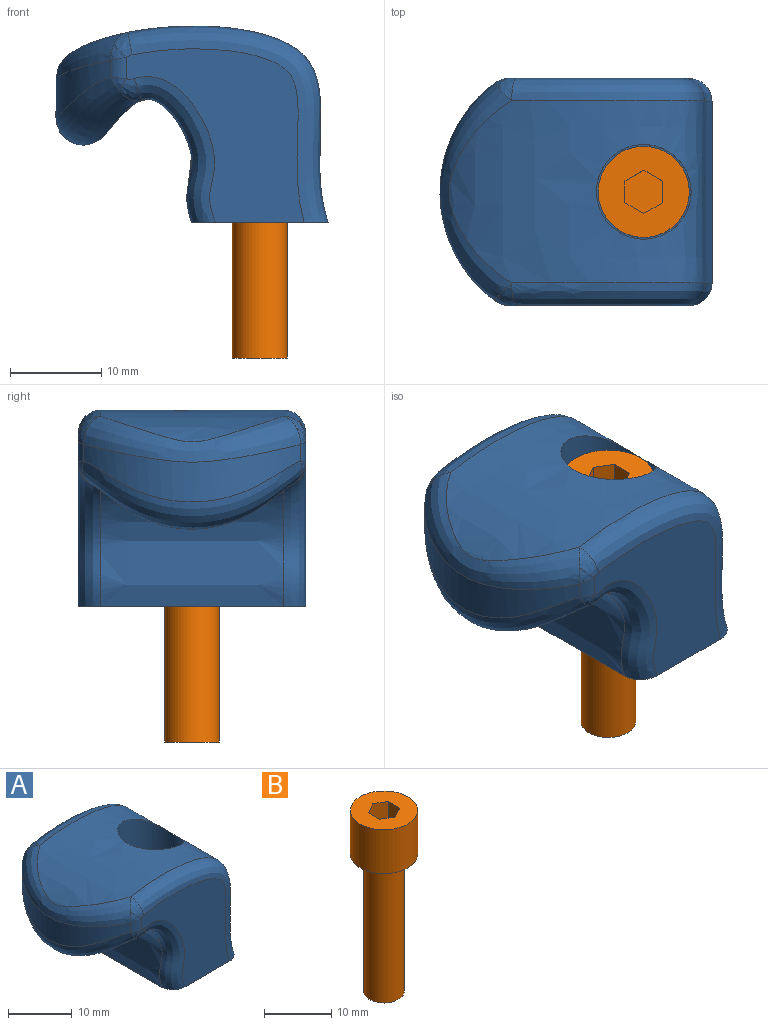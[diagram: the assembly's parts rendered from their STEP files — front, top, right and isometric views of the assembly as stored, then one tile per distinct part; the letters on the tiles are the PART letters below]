
ASSEMBLY  parts=2 mates=1
PART A: 25 faces, bbox 30.5x26.9x25.8 mm
  f0: extruded ~20x13.5mm, area 328.2mm2, adj f4,f11,f12,f15
  f1: extruded ~28.88x21.55mm, area 787mm2, adj f4,f5,f9,f10,f23
  f2: plane 19.51x19.07mm, normal (0,-1,0), area 211.6mm2, adj f4,f9,f12,f14,f19,f24
  f3: plane 19.51x19.07mm, normal (0,1,0), area 211.6mm2, adj f4,f10,f11,f13,f18,f21
  f4: plane 25.36x15.36mm, normal (0,0,-1), area 341.1mm2, adj f0,f1,f2,f3,f7,f9,f10,f11
  f5: cylinder r=5.2mm len=10.4mm, axis (0,0,1), area 258.7mm2, adj f1,f6
  f6: plane 10.4x10.4mm, normal (0,0,1), area 56.7mm2, adj f5,f7
  f7: cylinder r=3mm len=10mm, axis (0,0,1), area 188.5mm2, adj f4,f6
  f8: cylinder r=14.88mm len=23.8mm, axis (0,0,1), area 93.9mm2, adj f15,f18,f19,f23
  f9: bspline ~23.08x22.86mm, area 146.3mm2, adj f1,f2,f4,f24
  f10: bspline ~23.08x22.86mm, area 146.3mm2, adj f1,f3,f4,f21
  f11: bspline ~19.91x10.37mm, area 71.6mm2, adj f0,f3,f4,f13
  f12: bspline ~19.91x10.37mm, area 71.6mm2, adj f0,f2,f4,f14
  f13: bspline ~3.05x3.01mm, area 5mm2, adj f3,f11,f15,f16
  f14: bspline ~3.22x3.01mm, area 5mm2, adj f2,f12,f15,f17
  f15: bspline ~26.46x13.18mm, area 190.1mm2, adj f0,f8,f13,f14,f16,f17
  f16: bspline ~2.45x2.04mm, area 1.1mm2, adj f13,f15,f18
  f17: bspline ~2.45x2.04mm, area 1.1mm2, adj f14,f15,f19
  f18: cylinder r=3mm len=2.33mm, axis (0,0,1), area 4mm2, adj f3,f8,f16,f20
  f19: cylinder r=3mm len=2.33mm, axis (0,0,1), area 4mm2, adj f2,f8,f17,f22
  f20: bspline ~2.18x2.1mm, area 1.3mm2, adj f18,f21,f23
  f21: bspline ~3.18x2.85mm, area 4.5mm2, adj f3,f10,f20,f23
  f22: bspline ~2.18x2.1mm, area 1.3mm2, adj f19,f23,f24
  f23: bspline ~26.37x8.94mm, area 95.3mm2, adj f1,f8,f20,f21,f22,f24
  f24: bspline ~2.98x2.66mm, area 4.5mm2, adj f2,f9,f22,f23
PART B: 12 faces, bbox 10x10x33 mm
  f0: plane 10x10mm, normal (0,0,1), area 63.7mm2, adj f3,f5,f6,f7,f8,f9,f10
  f1: cylinder r=3mm len=25mm, axis (0,0,-1), area 471.2mm2, adj f2,f4
  f2: plane 6x6mm, normal (0,0,-1), area 28.3mm2, adj f1
  f3: cylinder r=5mm len=10mm, axis (0,0,-1), area 251.3mm2, adj f0,f4
  f4: plane 10x10mm, normal (0,0,-1), area 50.3mm2, adj f1,f3
  f5: plane 7x2.08mm, normal (-0.49,0.87,0), area 16.7mm2, adj f0,f6,f10,f11
  f6: plane 7x2.39mm, normal (-1,0.01,0), area 16.7mm2, adj f0,f5,f7,f11
  f7: plane 7x2.06mm, normal (-0.51,-0.86,0), area 16.7mm2, adj f0,f6,f8,f11
  f8: plane 7x2.08mm, normal (0.49,-0.87,0), area 16.7mm2, adj f0,f7,f9,f11
  f9: plane 7x2.39mm, normal (1,-0.01,0), area 16.7mm2, adj f0,f8,f10,f11
  f10: plane 7x2.06mm, normal (0.51,0.86,0), area 16.7mm2, adj f0,f5,f9,f11
  f11: plane 4.77x4.15mm, normal (0,0,1), area 14.8mm2, adj f5,f6,f7,f8,f9,f10
PLACE A t=(-6.82,16.04,0.21)mm fixed
PLACE B t=(0.68,3.54,-14.69)mm
MATE slider B.f1 <-> A.f5  axis (0,0,-1) through (0.68,3.54,-14.69)mm
